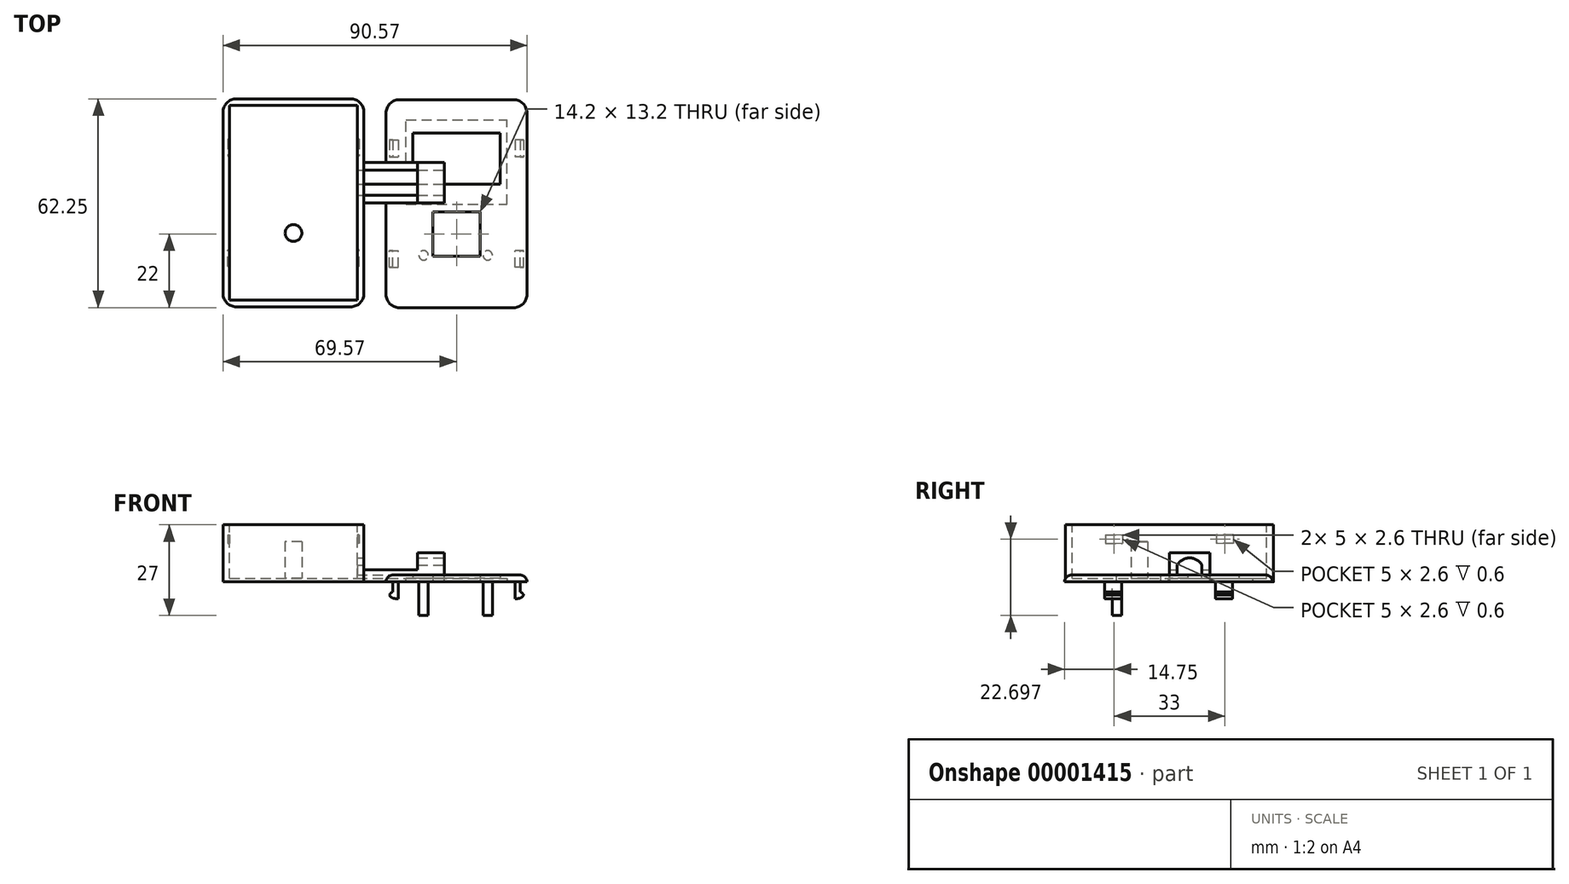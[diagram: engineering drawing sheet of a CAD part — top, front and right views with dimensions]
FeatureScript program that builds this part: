
annotation { "Feature Type Name" : "Feature", "Feature Type Description" : "" }
export const myFeature = defineFeature(function(context is Context, id is Id, definition is map)
    precondition{}
    {
        {
            var Q0;
            Q0=qCreatedBy(makeId("Top.planeOp"),FACE);
            var sketch = newSketch(context, id + "F0", { "sketchPlane" : qUnion([Q0])});
            skLineSegment(sketch, "E0.bottom", {"start": v(-21, 33.4) * mm, "end": v(21, 33.4) * mm});
            skLineSegment(sketch, "E0.top", {"start": v(-21, -28.6) * mm, "end": v(21, -28.6) * mm});
            skLineSegment(sketch, "E0.left", {"start": v(-21, 33.4) * mm, "end": v(-21, -28.6) * mm});
            skLineSegment(sketch, "E0.right", {"start": v(21, 33.4) * mm, "end": v(21, -28.6) * mm});
            skLineSegment(sketch, "E1", {"start": v(0, 33.4) * mm, "end": v(0, 23.4) * mm, "construction": true});
            skLineSegment(sketch, "E2.bottom", {"start": v(-13, 23.4) * mm, "end": v(13, 23.4) * mm});
            skLineSegment(sketch, "E2.top", {"start": v(-13, 8.2) * mm, "end": v(13, 8.2) * mm});
            skLineSegment(sketch, "E2.left", {"start": v(-13, 23.4) * mm, "end": v(-13, 8.2) * mm});
            skLineSegment(sketch, "E2.right", {"start": v(13, 23.4) * mm, "end": v(13, 8.2) * mm});
            skLineSegment(sketch, "E3", {"start": v(0, 33.4) * mm, "end": v(0, -6.6) * mm, "construction": true});
            skLineSegment(sketch, "E4.bottom", {"start": v(-7.1, -13.2) * mm, "end": v(7.1, -13.2) * mm});
            skLineSegment(sketch, "E4.top", {"start": v(-7.1, 0) * mm, "end": v(7.1, 0) * mm});
            skLineSegment(sketch, "E4.left", {"start": v(-7.1, -13.2) * mm, "end": v(-7.1, 0) * mm});
            skLineSegment(sketch, "E4.right", {"start": v(7.1, -13.2) * mm, "end": v(7.1, 0) * mm});
            skLineSegment(sketch, "E5", {"start": v(-7.1, -6.6) * mm, "end": v(0, -6.6) * mm, "construction": true});
            skLineSegment(sketch, "E6", {"start": v(0, -6.6) * mm, "end": v(0, -13.2) * mm, "construction": true});
            skLineSegment(sketch, "E7", {"start": v(0, -13.2) * mm, "end": v(-9.4, -13.2) * mm, "construction": true});
            skLineSegment(sketch, "E8", {"start": v(0, -13.2) * mm, "end": v(9.7, -13.2) * mm, "construction": true});
            skLineSegment(sketch, "E9", {"start": v(0, -6.6) * mm, "end": v(0, -28.6) * mm, "construction": true});
            skSolve(sketch);
        }
        {
            var Q0;
            Q0=makeQuery(id+"F0.imprint","IMPRINT",FACE,{"disambiguationData":[TD([[makeQuery(id+"F0.imprint","IMPRINT",EDGE,{"derivedFrom":sQuery(id+"F0.wireOp",EDGE,"E0.bottom")}),-1.0]])]});
            extrude(context, id + "F1", {"entities" : qUnion([Q0]), "depth" : 2 * mm});
        }
        {
            var Q0;
            Q0=makeQuery(id+"F1.opExtrude","CAP_FACE",FACE,{"disambiguationData":[OSD([sQuery(id+"F0.wireOp",EDGE,"E0.bottom"),sQuery(id+"F0.wireOp",EDGE,"E0.top"),sQuery(id+"F0.wireOp",EDGE,"E0.left"),sQuery(id+"F0.wireOp",EDGE,"E0.right"),sQuery(id+"F0.wireOp",EDGE,"E2.bottom"),sQuery(id+"F0.wireOp",EDGE,"E2.top"),sQuery(id+"F0.wireOp",EDGE,"E2.left"),sQuery(id+"F0.wireOp",EDGE,"E2.right"),sQuery(id+"F0.wireOp",EDGE,"E4.bottom"),sQuery(id+"F0.wireOp",EDGE,"E4.top"),sQuery(id+"F0.wireOp",EDGE,"E4.left"),sQuery(id+"F0.wireOp",EDGE,"E4.right")])],"isStart":true});
            var sketch = newSketch(context, id + "F2", { "sketchPlane" : qUnion([Q0])});
            skLineSegment(sketch, "E10", {"start": v(-21, 16.6) * mm, "end": v(-19, 16.6) * mm, "construction": true});
            skLineSegment(sketch, "E11.bottom", {"start": v(-19, 16.6) * mm, "end": v(-17.4, 16.6) * mm});
            skLineSegment(sketch, "E11.top", {"start": v(-19, 11.6) * mm, "end": v(-17.4, 11.6) * mm});
            skLineSegment(sketch, "E11.left", {"start": v(-19, 16.6) * mm, "end": v(-19, 11.6) * mm});
            skLineSegment(sketch, "E11.right", {"start": v(-17.4, 16.6) * mm, "end": v(-17.4, 11.6) * mm});
            skLineSegment(sketch, "E12", {"start": v(-18.2, 16.6) * mm, "end": v(-18.2, 28.6) * mm, "construction": true});
            skLineSegment(sketch, "E13", {"start": v(21, -2.4) * mm, "end": v(-21, -2.4) * mm, "construction": true});
            skSolve(sketch);
        }
        {
            var Q0;
            Q0 = qSketchRegion(id + "F2", true);
            extrude(context, id + "F3", {"entities" : qUnion([Q0]), "depth" : 5 * mm});
        }
        {
            var Q0;
            Q0=makeQuery(id+"F3.opExtrude","SWEPT_FACE",FACE,{"disambiguationData":[OSD([sQuery(id+"F2.wireOp",EDGE,"E11.left")])]});
            var sketch = newSketch(context, id + "F4", { "sketchPlane" : qUnion([Q0])});
            skLineSegment(sketch, "E14.bottom", {"start": v(11.6, -3) * mm, "end": v(16.6, -3) * mm});
            skLineSegment(sketch, "E14.top", {"start": v(11.6, -5) * mm, "end": v(16.6, -5) * mm});
            skLineSegment(sketch, "E14.left", {"start": v(11.6, -3) * mm, "end": v(11.6, -5) * mm});
            skLineSegment(sketch, "E14.right", {"start": v(16.6, -3) * mm, "end": v(16.6, -5) * mm});
            skSolve(sketch);
        }
        {
            var Q0;
            Q0 = qSketchRegion(id + "F4", true);
            extrude(context, id + "F5", {"entities" : qUnion([Q0]), "operationType" : NewBodyOperationType.ADD, "depth" : 1.2 * mm});
        }
        {
            var Q0;
            Q0=makeQuery(id+"F5.opExtrude","CAP_EDGE",EDGE,{"disambiguationData":[OSD([sQuery(id+"F4.wireOp",EDGE,"E14.bottom")])],"isStart":false});
            var Q1;
            Q1=makeQuery(id+"F5.opExtrude","CAP_EDGE",EDGE,{"disambiguationData":[OSD([sQuery(id+"F4.wireOp",EDGE,"E14.top")])],"isStart":false});
            fillet(context, id + "F6", {"entities" : qUnion([Q0, Q1]), "radius" : 2 * mm, "tangentPropagation" : true, "allowEdgeOverflow" : false});
        }
        {
            var Q0;
            Q0=makeQuery(id+"F3.opExtrude","SWEPT_BODY",BODY,{"disambiguationData":[OSD([sQuery(id+"F2.wireOp",EDGE,"E11.bottom"),sQuery(id+"F2.wireOp",EDGE,"E11.top"),sQuery(id+"F2.wireOp",EDGE,"E11.left"),sQuery(id+"F2.wireOp",EDGE,"E11.right")])]});
            var Q1;
            Q1=qCreatedBy(makeId("Right.planeOp"),FACE);
            mirror(context, id + "F7", {"entities" : qUnion([Q0]), "mirrorPlane" : qUnion([Q1])});
        }
        {
            var Q0;
            Q0=makeQuery(id+"F1.opExtrude","CAP_FACE",FACE,{"disambiguationData":[OSD([sQuery(id+"F0.wireOp",EDGE,"E0.bottom"),sQuery(id+"F0.wireOp",EDGE,"E0.top"),sQuery(id+"F0.wireOp",EDGE,"E0.left"),sQuery(id+"F0.wireOp",EDGE,"E0.right"),sQuery(id+"F0.wireOp",EDGE,"E2.bottom"),sQuery(id+"F0.wireOp",EDGE,"E2.top"),sQuery(id+"F0.wireOp",EDGE,"E2.left"),sQuery(id+"F0.wireOp",EDGE,"E2.right"),sQuery(id+"F0.wireOp",EDGE,"E4.bottom"),sQuery(id+"F0.wireOp",EDGE,"E4.top"),sQuery(id+"F0.wireOp",EDGE,"E4.left"),sQuery(id+"F0.wireOp",EDGE,"E4.right")])],"isStart":true});
            var sketch = newSketch(context, id + "F8", { "sketchPlane" : qUnion([Q0])});
            skLineSegment(sketch, "E15.bottom", {"start": v(-15, -2.2) * mm, "end": v(15, -2.2) * mm});
            skLineSegment(sketch, "E15.top", {"start": v(-15, -27.4) * mm, "end": v(15, -27.4) * mm});
            skLineSegment(sketch, "E15.left", {"start": v(-15, -2.2) * mm, "end": v(-15, -27.4) * mm});
            skLineSegment(sketch, "E15.right", {"start": v(15, -2.2) * mm, "end": v(15, -27.4) * mm});
            skLineSegment(sketch, "E16", {"start": v(-0.95, -8.2) * mm, "end": v(-0.95, -2.2) * mm, "construction": true});
            skLineSegment(sketch, "E17", {"start": v(-15, -15.05) * mm, "end": v(-13, -15.05) * mm, "construction": true});
            skLineSegment(sketch, "E18", {"start": v(13, -15.78) * mm, "end": v(15, -15.78) * mm, "construction": true});
            skLineSegment(sketch, "E19", {"start": v(1.73, -23.4) * mm, "end": v(1.73, -27.4) * mm, "construction": true});
            skSolve(sketch);
        }
        {
            var Q0;
            {var subQ3=makeQuery(id+"F8.imprint","IMPRINT",EDGE,{"derivedFrom":makeQuery(id+"F1.opExtrude","CAP_EDGE",EDGE,{"disambiguationData":[OSD([sQuery(id+"F0.wireOp",EDGE,"E2.bottom")])],"isStart":true})});Q0=qUnion([makeQuery(id+"F8.imprint","IMPRINT",FACE,{"disambiguationData":[TD([[subQ3,1.0]])]}),makeQuery(id+"F8.imprint","IMPRINT",FACE,{"disambiguationData":[TD([[makeQuery(id+"F8.imprint","IMPRINT",EDGE,{"derivedFrom":sQuery(id+"F8.wireOp",EDGE,"E15.bottom")}),-1.0]])]})]);}
            extrude(context, id + "F9", {"entities" : qUnion([Q0]), "operationType" : NewBodyOperationType.REMOVE, "oppositeDirection" : true, "depth" : 1 * mm});
        }
        {
            var Q0;
            Q0=qCreatedBy(makeId("Top.planeOp"),FACE);
            var sketch = newSketch(context, id + "F10", { "sketchPlane" : qUnion([Q0])});
            skLineSegment(sketch, "E20.bottom", {"start": v(-48.57, -28.35) * mm, "end": v(-27.57, -28.35) * mm});
            skLineSegment(sketch, "E20.top", {"start": v(-48.57, 33.65) * mm, "end": v(-27.57, 33.65) * mm});
            skLineSegment(sketch, "E20.left", {"start": v(-48.57, -28.35) * mm, "end": v(-48.57, 33.65) * mm});
            skLineSegment(sketch, "E20.right", {"start": v(-27.57, -28.35) * mm, "end": v(-27.57, 33.65) * mm});
            skLineSegment(sketch, "E21", {"start": v(-69.57, 44.74) * mm, "end": v(-27.57, 44.74) * mm, "construction": true});
            skLineSegment(sketch, "E22", {"start": v(-48.57, 44.74) * mm, "end": v(-48.57, 33.65) * mm, "construction": true});
            skLineSegment(sketch, "E23", {"start": v(-27.57, 44.74) * mm, "end": v(-27.57, 33.65) * mm, "construction": true});
            skSolve(sketch);
        }
        {
            var Q0;
            Q0=makeQuery(id+"F10.imprint","IMPRINT",FACE,{"disambiguationData":[TD([[makeQuery(id+"F10.imprint","IMPRINT",EDGE,{"derivedFrom":sQuery(id+"F10.wireOp",EDGE,"E20.bottom")}),1.0]])]});
            extrude(context, id + "F11", {"entities" : qUnion([Q0]), "depth" : 17 * mm});
        }
        {
            var Q0;
            Q0=makeQuery(id+"F11.opExtrude","CAP_FACE",FACE,{"disambiguationData":[OSD([sQuery(id+"F10.wireOp",EDGE,"E20.bottom"),sQuery(id+"F10.wireOp",EDGE,"E20.top"),sQuery(id+"F10.wireOp",EDGE,"E20.left"),sQuery(id+"F10.wireOp",EDGE,"E20.right")])],"isStart":false});
            var sketch = newSketch(context, id + "F12", { "sketchPlane" : qUnion([Q0])});
            skLineSegment(sketch, "E24.0", {"start": v(-48.57, 31.65) * mm, "end": v(-29.57, 31.65) * mm});
            skLineSegment(sketch, "E24.1", {"start": v(-48.57, -26.35) * mm, "end": v(-48.57, 31.65) * mm});
            skLineSegment(sketch, "E24.2", {"start": v(-48.57, -26.35) * mm, "end": v(-29.57, -26.35) * mm});
            skLineSegment(sketch, "E24.3", {"start": v(-29.57, -26.35) * mm, "end": v(-29.57, 31.65) * mm});
            skLineSegment(sketch, "E25", {"start": v(-39.52, -28.35) * mm, "end": v(-39.52, -26.35) * mm, "construction": true});
            skLineSegment(sketch, "E26", {"start": v(-40.91, 33.65) * mm, "end": v(-40.91, 31.65) * mm, "construction": true});
            skLineSegment(sketch, "E27", {"start": v(-29.57, 10.34) * mm, "end": v(-27.57, 10.34) * mm, "construction": true});
            skSolve(sketch);
        }
        {
            var Q0;
            Q0=makeQuery(id+"F12.imprint","IMPRINT",FACE,{"disambiguationData":[TD([[makeQuery(id+"F12.imprint","IMPRINT",EDGE,{"derivedFrom":sQuery(id+"F12.wireOp",EDGE,"E24.0")}),-1.0]])]});
            extrude(context, id + "F13", {"entities" : qUnion([Q0]), "operationType" : NewBodyOperationType.REMOVE, "oppositeDirection" : true, "depth" : (17 - 1) * mm});
        }
        {
            var Q0;
            Q0=makeQuery(id+"F13.boolean.opBoolean","COPY",FACE,{"derivedFrom":makeQuery(id+"F13.opExtrude","SWEPT_FACE",FACE,{"disambiguationData":[OSD([sQuery(id+"F12.wireOp",EDGE,"E24.3")])]})});
            var sketch = newSketch(context, id + "F14", { "sketchPlane" : qUnion([Q0])});
            skLineSegment(sketch, "E28", {"start": v(16.35, 17) * mm, "end": v(16.35, 14) * mm, "construction": true});
            skLineSegment(sketch, "E29.bottom", {"start": v(16.35, 14) * mm, "end": v(11.35, 14) * mm});
            skLineSegment(sketch, "E29.top", {"start": v(16.35, 11.4) * mm, "end": v(11.35, 11.4) * mm});
            skLineSegment(sketch, "E29.left", {"start": v(16.35, 14) * mm, "end": v(16.35, 11.4) * mm});
            skLineSegment(sketch, "E29.right", {"start": v(11.35, 14) * mm, "end": v(11.35, 11.4) * mm});
            skLineSegment(sketch, "E30.0", {"start": v(28.35, 17) * mm, "end": v(28.35, 0) * mm});
            skLineSegment(sketch, "E31", {"start": v(16.35, 12.7) * mm, "end": v(28.35, 12.7) * mm, "construction": true});
            skLineSegment(sketch, "E32.0", {"start": v(16.6, 0) * mm, "end": v(28.6, 0) * mm, "construction": true});
            skLineSegment(sketch, "E33", {"start": v(-2.65, 17) * mm, "end": v(-2.65, 1) * mm, "construction": true});
            skLineSegment(sketch, "E34.MirrorCS", {"start": v(-21.65, 14) * mm, "end": v(-16.65, 14) * mm});
            skLineSegment(sketch, "E35.MirrorCS", {"start": v(-16.65, 14) * mm, "end": v(-16.65, 11.4) * mm});
            skLineSegment(sketch, "E36.MirrorCS", {"start": v(-21.65, 11.4) * mm, "end": v(-16.65, 11.4) * mm});
            skLineSegment(sketch, "E37.MirrorCS", {"start": v(-21.65, 14) * mm, "end": v(-21.65, 11.4) * mm});
            skSolve(sketch);
        }
        {
            var Q0;
            Q0 = qSketchRegion(id + "F14", true);
            extrude(context, id + "F15", {"entities" : qUnion([Q0]), "operationType" : NewBodyOperationType.REMOVE, "oppositeDirection" : true, "depth" : .6 * mm});
        }
        {
            var Q0;
            Q0=makeQuery(id+"F11.opExtrude","SWEPT_FACE",FACE,{"disambiguationData":[OSD([sQuery(id+"F10.wireOp",EDGE,"E20.left")])]});
            cPlane(context, id + "F16", {"entities" : qUnion([Q0]), "cplaneType" : CPlaneType.OFFSET, "offset" : 0 * mm, "width" : 150 * mm, "height" : 150 * mm});
        }
        {
            var Q0;
            Q0=makeQuery(id+"F11.opExtrude","SWEPT_EDGE",EDGE,{"disambiguationData":[OSD([sQuery(id+"F10.wireOp",EDGE,"E20.top"),sQuery(id+"F10.wireOp",EDGE,"E20.right")])]});
            var Q1;
            Q1=makeQuery(id+"F11.opExtrude","SWEPT_EDGE",EDGE,{"disambiguationData":[OSD([sQuery(id+"F10.wireOp",EDGE,"E20.bottom"),sQuery(id+"F10.wireOp",EDGE,"E20.right")])]});
            fillet(context, id + "F17", {"entities" : qUnion([Q0, Q1]), "radius" : 4 * mm, "tangentPropagation" : true, "allowEdgeOverflow" : false});
        }
        {
            var Q0;
            Q0=makeQuery(id+"F11.opExtrude","SWEPT_BODY",BODY,{"disambiguationData":[OSD([sQuery(id+"F10.wireOp",EDGE,"E20.bottom"),sQuery(id+"F10.wireOp",EDGE,"E20.top"),sQuery(id+"F10.wireOp",EDGE,"E20.left"),sQuery(id+"F10.wireOp",EDGE,"E20.right")])]});
            var Q1;
            Q1=qCreatedBy(id+"F16.planeOp",FACE);
            mirror(context, id + "F18", {"entities" : qUnion([Q0]), "mirrorPlane" : qUnion([Q1])});
        }
        {
            var Q0;
            Q0=makeQuery(id+"F1.opExtrude","SWEPT_EDGE",EDGE,{"disambiguationData":[OSD([sQuery(id+"F0.wireOp",EDGE,"E0.bottom"),sQuery(id+"F0.wireOp",EDGE,"E0.right")])]});
            var Q1;
            Q1=makeQuery(id+"F1.opExtrude","SWEPT_EDGE",EDGE,{"disambiguationData":[OSD([sQuery(id+"F0.wireOp",EDGE,"E0.top"),sQuery(id+"F0.wireOp",EDGE,"E0.right")])]});
            var Q2;
            Q2=makeQuery(id+"F1.opExtrude","SWEPT_EDGE",EDGE,{"disambiguationData":[OSD([sQuery(id+"F0.wireOp",EDGE,"E0.top"),sQuery(id+"F0.wireOp",EDGE,"E0.left")])]});
            var Q3;
            Q3=makeQuery(id+"F1.opExtrude","SWEPT_EDGE",EDGE,{"disambiguationData":[OSD([sQuery(id+"F0.wireOp",EDGE,"E0.bottom"),sQuery(id+"F0.wireOp",EDGE,"E0.left")])]});
            fillet(context, id + "F19", {"entities" : qUnion([Q0, Q1, Q2, Q3]), "radius" : 4 * mm, "tangentPropagation" : true, "allowEdgeOverflow" : false});
        }
        {
            var Q0;
            Q0=makeQuery(id+"F1.opExtrude","CAP_EDGE",EDGE,{"disambiguationData":[OSD([sQuery(id+"F0.wireOp",EDGE,"E0.left")])],"isStart":false});
            var Q1;
            Q1=makeQuery(id+"F1.opExtrude","CAP_EDGE",EDGE,{"disambiguationData":[OSD([sQuery(id+"F0.wireOp",EDGE,"E0.top")])],"isStart":false});
            var Q2;
            Q2=makeQuery(id+"F1.opExtrude","CAP_EDGE",EDGE,{"disambiguationData":[OSD([sQuery(id+"F0.wireOp",EDGE,"E0.right")])],"isStart":false});
            var Q3;
            Q3=makeQuery(id+"F1.opExtrude","CAP_EDGE",EDGE,{"disambiguationData":[OSD([sQuery(id+"F0.wireOp",EDGE,"E0.bottom")])],"isStart":false});
            fillet(context, id + "F20", {"entities" : qUnion([Q0, Q1, Q2, Q3]), "radius" : 2 * mm, "tangentPropagation" : true, "allowEdgeOverflow" : false});
        }
        {
            var Q0;
            Q0=makeQuery(id+"F1.opExtrude","CAP_FACE",FACE,{"disambiguationData":[OSD([sQuery(id+"F0.wireOp",EDGE,"E0.bottom"),sQuery(id+"F0.wireOp",EDGE,"E0.top"),sQuery(id+"F0.wireOp",EDGE,"E0.left"),sQuery(id+"F0.wireOp",EDGE,"E0.right"),sQuery(id+"F0.wireOp",EDGE,"E2.bottom"),sQuery(id+"F0.wireOp",EDGE,"E2.top"),sQuery(id+"F0.wireOp",EDGE,"E2.left"),sQuery(id+"F0.wireOp",EDGE,"E2.right"),sQuery(id+"F0.wireOp",EDGE,"E4.bottom"),sQuery(id+"F0.wireOp",EDGE,"E4.top"),sQuery(id+"F0.wireOp",EDGE,"E4.left"),sQuery(id+"F0.wireOp",EDGE,"E4.right")])],"isStart":true});
            var sketch = newSketch(context, id + "F21", { "sketchPlane" : qUnion([Q0])});
            skCircle(sketch, "E38", {"center": v(-9.8, 13) * mm, "radius": 1.4 * mm});
            skCircle(sketch, "E39", {"center": v(9.3, 13) * mm, "radius": 1.4 * mm});
            skLineSegment(sketch, "E40", {"start": v(-7.1, 13.2) * mm, "end": v(-9.8, 13.2) * mm, "construction": true});
            skLineSegment(sketch, "E41", {"start": v(-9.8, 13) * mm, "end": v(-9.8, 13.2) * mm, "construction": true});
            skLineSegment(sketch, "E42", {"start": v(7.1, 13.2) * mm, "end": v(9.3, 13.2) * mm, "construction": true});
            skLineSegment(sketch, "E43", {"start": v(9.3, 13) * mm, "end": v(9.3, 13.2) * mm, "construction": true});
            skSolve(sketch);
        }
        {
            var Q0;
            {Q0=qUnion([makeQuery(id+"F21.imprint","IMPRINT",FACE,{"disambiguationData":[TD([[makeQuery(id+"F21.imprint","IMPRINT",EDGE,{"derivedFrom":sQuery(id+"F21.wireOp",EDGE,"E38")}),1.0]])]}),makeQuery(id+"F21.imprint","IMPRINT",FACE,{"disambiguationData":[TD([[makeQuery(id+"F21.imprint","IMPRINT",EDGE,{"derivedFrom":sQuery(id+"F21.wireOp",EDGE,"E39")}),1.0]])]})]);}
            extrude(context, id + "F22", {"entities" : qUnion([Q0]), "operationType" : NewBodyOperationType.ADD, "depth" : 10 * mm});
        }
        {
            var Q0;
            Q0=makeQuery(id+"F11.opExtrude","SWEPT_FACE",FACE,{"disambiguationData":[OSD([sQuery(id+"F10.wireOp",EDGE,"E20.right")])]});
            var sketch = newSketch(context, id + "F23", { "sketchPlane" : qUnion([Q0])});
            skLineSegment(sketch, "E44.bottom", {"start": v(2.65, 0) * mm, "end": v(14.65, 0) * mm});
            skLineSegment(sketch, "E44.top", {"start": v(2.65, 3.6) * mm, "end": v(14.65, 3.6) * mm});
            skLineSegment(sketch, "E44.left", {"start": v(2.65, 0) * mm, "end": v(2.65, 3.6) * mm});
            skLineSegment(sketch, "E44.right", {"start": v(14.65, 0) * mm, "end": v(14.65, 3.6) * mm});
            skLineSegment(sketch, "E45", {"start": v(14.65, 1.8) * mm, "end": v(29.65, 1.8) * mm, "construction": true});
            skSolve(sketch);
        }
        {
            var Q0;
            Q0=makeQuery(id+"F23.imprint","IMPRINT",FACE,{"disambiguationData":[TD([[makeQuery(id+"F23.imprint","IMPRINT",EDGE,{"derivedFrom":sQuery(id+"F23.wireOp",EDGE,"E44.bottom")}),1.0]])]});
            extrude(context, id + "F24", {"entities" : qUnion([Q0]), "operationType" : NewBodyOperationType.ADD, "depth" : 24 * mm});
        }
        {
            var Q0;
            Q0=makeQuery(id+"F24.opExtrude","SWEPT_FACE",FACE,{"disambiguationData":[OSD([sQuery(id+"F23.wireOp",EDGE,"E44.top")])]});
            var sketch = newSketch(context, id + "F25", { "sketchPlane" : qUnion([Q0])});
            skLineSegment(sketch, "E46.bottom", {"start": v(-3.57, 2.65) * mm, "end": v(-11.57, 2.65) * mm});
            skLineSegment(sketch, "E46.top", {"start": v(-3.57, 14.65) * mm, "end": v(-11.57, 14.65) * mm});
            skLineSegment(sketch, "E46.left", {"start": v(-3.57, 2.65) * mm, "end": v(-3.57, 14.65) * mm});
            skLineSegment(sketch, "E46.right", {"start": v(-11.57, 2.65) * mm, "end": v(-11.57, 14.65) * mm});
            skSolve(sketch);
        }
        {
            var Q0;
            Q0=makeQuery(id+"F25.imprint","IMPRINT",FACE,{"disambiguationData":[TD([[makeQuery(id+"F25.imprint","IMPRINT",EDGE,{"derivedFrom":sQuery(id+"F25.wireOp",EDGE,"E46.bottom")}),-1.0]])]});
            extrude(context, id + "F26", {"entities" : qUnion([Q0]), "operationType" : NewBodyOperationType.ADD, "depth" : 5 * mm});
        }
        {
            var Q0;
            Q0=makeQuery(id+"F26.boolean.opBoolean","MERGE",FACE,{"derivedFrom":[makeQuery(id+"F24.opExtrude","CAP_FACE",FACE,{"disambiguationData":[OSD([sQuery(id+"F23.wireOp",EDGE,"E44.bottom"),sQuery(id+"F23.wireOp",EDGE,"E44.top"),sQuery(id+"F23.wireOp",EDGE,"E44.left"),sQuery(id+"F23.wireOp",EDGE,"E44.right")])],"isStart":false}),makeQuery(id+"F26.opExtrude","SWEPT_FACE",FACE,{"disambiguationData":[OSD([sQuery(id+"F25.wireOp",EDGE,"E46.left")])]})]});
            var sketch = newSketch(context, id + "F27", { "sketchPlane" : qUnion([Q0])});
            skLineSegment(sketch, "E47", {"start": v(8.65, 1) * mm, "end": v(8.65, 0) * mm, "construction": true});
            skLineSegment(sketch, "E48.bottom", {"start": v(4.95, 1) * mm, "end": v(12.35, 1) * mm});
            skLineSegment(sketch, "E48.top", {"start": v(4.95, 5) * mm, "end": v(12.35, 5) * mm});
            skLineSegment(sketch, "E48.left", {"start": v(4.95, 1) * mm, "end": v(4.95, 5) * mm});
            skLineSegment(sketch, "E48.right", {"start": v(12.35, 1) * mm, "end": v(12.35, 5) * mm});
            skArc(sketch, "E49", {"start": v(12.35, 5) * mm, "mid": v(8.65, 7.1) * mm, "end": v(4.95, 5) * mm});
            skSolve(sketch);
        }
        {
            var Q0;
            {var subQ0=makeQuery(id+"F27.imprint","IMPRINT",EDGE,{"derivedFrom":sQuery(id+"F27.wireOp",EDGE,"E48.top")});Q0=qUnion([makeQuery(id+"F27.imprint","IMPRINT",FACE,{"disambiguationData":[TD([[makeQuery(id+"F27.imprint","IMPRINT",EDGE,{"derivedFrom":sQuery(id+"F27.wireOp",EDGE,"E48.bottom")}),1.0]])]}),makeQuery(id+"F27.imprint","IMPRINT",FACE,{"disambiguationData":[TD([[subQ0,1.0]])]})]);}
            var Q1;
            Q1=makeQuery(id+"F13.boolean.opBoolean","COPY",FACE,{"derivedFrom":makeQuery(id+"F13.opExtrude","SWEPT_FACE",FACE,{"disambiguationData":[OSD([sQuery(id+"F12.wireOp",EDGE,"E24.3")])]})});
            extrude(context, id + "F28", {"entities" : qUnion([Q0]), "operationType" : NewBodyOperationType.REMOVE, "endBound" : BoundingType.UP_TO_SURFACE, "oppositeDirection" : true, "endBoundEntityFace" : qUnion([Q1]), "depth" : 25 * mm});
        }
        {
            var Q0;
            Q0=makeQuery(id+"F28.boolean.opBoolean","MERGE",FACE,{"derivedFrom":[makeQuery(id+"F13.boolean.opBoolean","COPY",FACE,{"derivedFrom":makeQuery(id+"F13.opExtrude","CAP_FACE",FACE,{"disambiguationData":[OSD([sQuery(id+"F12.wireOp",EDGE,"E24.0"),sQuery(id+"F12.wireOp",EDGE,"E24.1"),sQuery(id+"F12.wireOp",EDGE,"E24.2"),sQuery(id+"F12.wireOp",EDGE,"E24.3")])],"isStart":false})}),makeQuery(id+"F28.opExtrude","SWEPT_FACE",FACE,{"disambiguationData":[OSD([sQuery(id+"F27.wireOp",EDGE,"E48.bottom")])]})]});
            var sketch = newSketch(context, id + "F29", { "sketchPlane" : qUnion([Q0])});
            skCircle(sketch, "E50", {"center": v(-48.57, -6.35) * mm, "radius": 2.5 * mm});
            skLineSegment(sketch, "E51.0", {"start": v(-48.57, -28.35) * mm, "end": v(-27.57, -28.35) * mm});
            skLineSegment(sketch, "E52", {"start": v(-48.57, -6.35) * mm, "end": v(-48.57, -28.35) * mm, "construction": true});
            skSolve(sketch);
        }
        {
            var Q0;
            {var subQ0=makeQuery(id+"F13.boolean.opBoolean","COPY",EDGE,{"derivedFrom":makeQuery(id+"F13.opExtrude","CAP_EDGE",EDGE,{"disambiguationData":[OSD([sQuery(id+"F12.wireOp",EDGE,"E24.1")])],"isStart":false})});var subQ1=sQuery(id+"F29.wireOp",EDGE,"E50");var subQ3=makeQuery(id+"F29.imprint","INTERSECT",VERTEX,{"disambiguationData":[OD(0.0)],"derivedFrom":[subQ0,subQ1]});Q0=makeQuery(id+"F29.imprint","IMPRINT",FACE,{"disambiguationData":[TD([[makeQuery(id+"F29.imprint","IMPRINT",EDGE,{"disambiguationData":[TD([[subQ3,1.0]])],"derivedFrom":subQ1}),1.0]])]});}
            var Q1;
            {var subQ0=makeQuery(id+"F13.boolean.opBoolean","COPY",EDGE,{"derivedFrom":makeQuery(id+"F13.opExtrude","CAP_EDGE",EDGE,{"disambiguationData":[OSD([sQuery(id+"F12.wireOp",EDGE,"E24.1")])],"isStart":false})});var subQ1=sQuery(id+"F29.wireOp",EDGE,"E50");var subQ3=makeQuery(id+"F29.imprint","INTERSECT",VERTEX,{"disambiguationData":[OD(0.0)],"derivedFrom":[subQ0,subQ1]});Q1=makeQuery(id+"F29.imprint","IMPRINT",FACE,{"disambiguationData":[TD([[makeQuery(id+"F29.imprint","IMPRINT",EDGE,{"disambiguationData":[TD([[subQ3,-1.0]])],"derivedFrom":subQ1}),1.0]])]});}
            extrude(context, id + "F30", {"entities" : qUnion([Q0, Q1]), "operationType" : NewBodyOperationType.ADD, "depth" : 11 * mm});
        }
        {
            var Q0;
            Q0=makeQuery(id+"F1.opExtrude","SWEPT_BODY",BODY,{"disambiguationData":[OSD([sQuery(id+"F0.wireOp",EDGE,"E0.bottom"),sQuery(id+"F0.wireOp",EDGE,"E0.top"),sQuery(id+"F0.wireOp",EDGE,"E0.left"),sQuery(id+"F0.wireOp",EDGE,"E0.right"),sQuery(id+"F0.wireOp",EDGE,"E2.bottom"),sQuery(id+"F0.wireOp",EDGE,"E2.top"),sQuery(id+"F0.wireOp",EDGE,"E2.left"),sQuery(id+"F0.wireOp",EDGE,"E2.right"),sQuery(id+"F0.wireOp",EDGE,"E4.bottom"),sQuery(id+"F0.wireOp",EDGE,"E4.top"),sQuery(id+"F0.wireOp",EDGE,"E4.left"),sQuery(id+"F0.wireOp",EDGE,"E4.right")])]});
            var Q1;
            Q1=makeQuery(id+"F3.opExtrude","SWEPT_BODY",BODY,{"disambiguationData":[OSD([sQuery(id+"F2.wireOp",EDGE,"E11.bottom"),sQuery(id+"F2.wireOp",EDGE,"E11.top"),sQuery(id+"F2.wireOp",EDGE,"E11.left"),sQuery(id+"F2.wireOp",EDGE,"E11.right")])]});
            var Q2;
            Q2=makeQuery(id+"F7.opPattern","COPY",BODY,{"derivedFrom":makeQuery(id+"F3.opExtrude","SWEPT_BODY",BODY,{"disambiguationData":[OSD([sQuery(id+"F2.wireOp",EDGE,"E11.bottom"),sQuery(id+"F2.wireOp",EDGE,"E11.top"),sQuery(id+"F2.wireOp",EDGE,"E11.left"),sQuery(id+"F2.wireOp",EDGE,"E11.right")])]}),"instanceName":"1"});
            var Q3;
            Q3=makeQuery(id+"F3.opExtrude","SWEPT_BODY",BODY,{"disambiguationData":[OSD([sQuery(id+"F2.wireOp",EDGE,"e61529e6-9832-4a86-939e-d4a40a0d3fc60.MirrorCS"),sQuery(id+"F2.wireOp",EDGE,"c8aa3293-5f89-4f4d-96fb-824809e0a4a30.MirrorCS"),sQuery(id+"F2.wireOp",EDGE,"10f90e17-c9a4-45de-8557-0dcf797dd6540.MirrorCS"),sQuery(id+"F2.wireOp",EDGE,"daf5e375-9014-48b4-9dc4-4cb15065a8360.MirrorCS")])]});
            var Q4;
            Q4=makeQuery(id+"F5.opExtrude","SWEPT_BODY",BODY,{"disambiguationData":[OSD([sQuery(id+"F4.wireOp",EDGE,"37dfdb5e-1285-4759-9ba4-586cd9febcdf0.MirrorCS"),sQuery(id+"F4.wireOp",EDGE,"37dfdb5e-1285-4759-9ba4-586cd9febcdf1.MirrorCS"),sQuery(id+"F4.wireOp",EDGE,"37dfdb5e-1285-4759-9ba4-586cd9febcdf2.MirrorCS"),sQuery(id+"F4.wireOp",EDGE,"37dfdb5e-1285-4759-9ba4-586cd9febcdf3.MirrorCS")])]});
            transform(context, id + "F31", {"entities" : qUnion([Q0, Q1, Q2, Q3, Q4]), "transformType" : TransformType.TRANSLATION_3D, "dx" : 0 * mm, "dy" : 0 * mm, "dz" : 56.04 * mm, "makeCopy" : false});
        }
        {
            var Q0;
            Q0=sQuery(id+"F2.wireOp",EDGE,"E13");
            cPlane(context, id + "F32", {"entities" : qUnion([Q0]), "cplaneType" : CPlaneType.LINE_ANGLE, "offset" : 25 * mm, "angle" : 0 * degree, "width" : 150 * mm, "height" : 150 * mm});
        }
        {
            var Q0;
            Q0=makeQuery(id+"F7.opPattern","COPY",BODY,{"derivedFrom":makeQuery(id+"F3.opExtrude","SWEPT_BODY",BODY,{"disambiguationData":[OSD([sQuery(id+"F2.wireOp",EDGE,"E11.bottom"),sQuery(id+"F2.wireOp",EDGE,"E11.top"),sQuery(id+"F2.wireOp",EDGE,"E11.left"),sQuery(id+"F2.wireOp",EDGE,"E11.right")])]}),"instanceName":"1"});
            var Q1;
            Q1=makeQuery(id+"F3.opExtrude","SWEPT_BODY",BODY,{"disambiguationData":[OSD([sQuery(id+"F2.wireOp",EDGE,"E11.bottom"),sQuery(id+"F2.wireOp",EDGE,"E11.top"),sQuery(id+"F2.wireOp",EDGE,"E11.left"),sQuery(id+"F2.wireOp",EDGE,"E11.right")])]});
            var Q2;
            Q2=qCreatedBy(id+"F32.planeOp",FACE);
            mirror(context, id + "F33", {"operationType" : NewBodyOperationType.ADD, "entities" : qUnion([Q0, Q1]), "mirrorPlane" : qUnion([Q2])});
        }
    });
